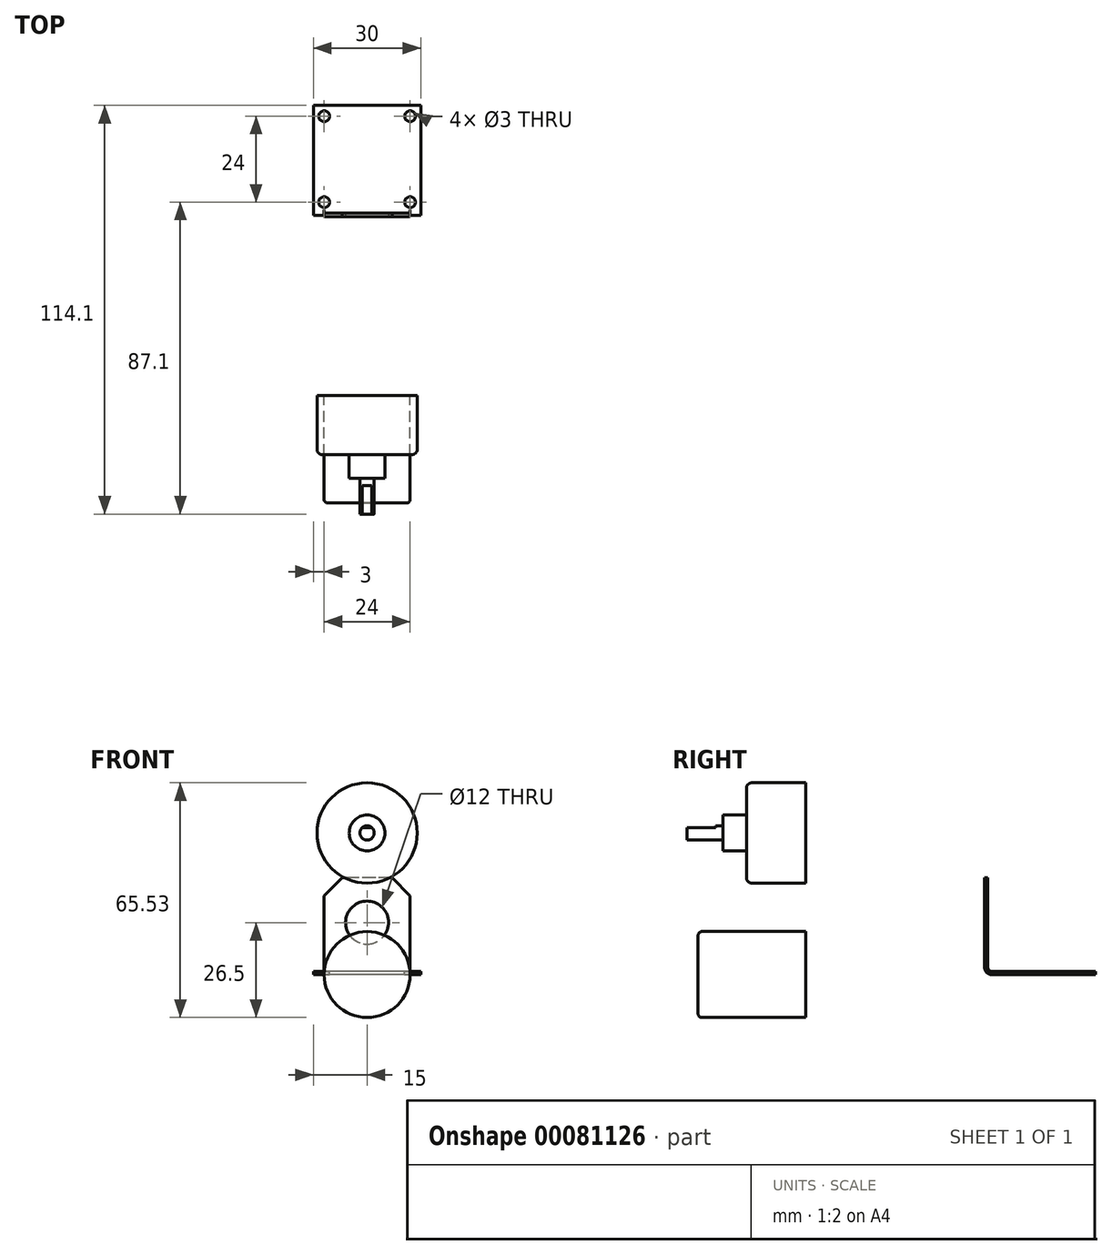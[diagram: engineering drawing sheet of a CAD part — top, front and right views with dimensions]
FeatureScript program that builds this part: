
annotation { "Feature Type Name" : "Feature", "Feature Type Description" : "" }
export const myFeature = defineFeature(function(context is Context, id is Id, definition is map)
    precondition{}
    {
        {
            var Q0;
            Q0=qCreatedBy(makeId("Front.planeOp"),FACE);
            var sketch = newSketch(context, id + "F0", { "sketchPlane" : qUnion([Q0])});
            skCircle(sketch, "E0", {"center": v(0, 0) * mm, "radius": 12 * mm});
            skSolve(sketch);
        }
        {
            var Q0;
            Q0=makeQuery(id+"F0.imprint","IMPRINT",FACE,{"disambiguationData":[TD([[makeQuery(id+"F0.imprint","IMPRINT",EDGE,{"derivedFrom":sQuery(id+"F0.wireOp",EDGE,"E0")}),1.0]])]});
            extrude(context, id + "F1", {"entities" : qUnion([Q0]), "depth" : 30 * mm});
        }
        {
            var Q0;
            Q0=makeQuery(id+"F1.opExtrude","CAP_EDGE",EDGE,{"disambiguationData":[OSD([sQuery(id+"F0.wireOp",EDGE,"E0")])],"isStart":false});
            fillet(context, id + "F2", {"entities" : qUnion([Q0]), "radius" : 1 * mm, "tangentPropagation" : true, "allowEdgeOverflow" : false});
        }
        {
            var Q0;
            Q0=qCreatedBy(makeId("Right.planeOp"),FACE);
            var sketch = newSketch(context, id + "F3", { "sketchPlane" : qUnion([Q0])});
            skLineSegment(sketch, "E1", {"start": v(81, 0) * mm, "end": v(51.9, 0) * mm});
            skLineSegment(sketch, "E2", {"start": v(50, 1.9) * mm, "end": v(50, 27) * mm});
            skLineSegment(sketch, "E3", {"start": v(50, 27) * mm, "end": v(50.9, 27) * mm});
            skLineSegment(sketch, "E4", {"start": v(50.9, 27) * mm, "end": v(50.9, 1.9) * mm});
            skLineSegment(sketch, "E5", {"start": v(51.9, 0.9) * mm, "end": v(81, 0.9) * mm});
            skLineSegment(sketch, "E6", {"start": v(81, 0.9) * mm, "end": v(81, 0) * mm});
            skPoint(sketch, "E7.visualSharp", {"position": v(50.9, 0.9) * mm});
            skArc(sketch, "E7.filletArc", {"start": v(50.9, 1.9) * mm, "mid": v(51.2, 1.2) * mm, "end": v(51.9, 0.9) * mm});
            skPoint(sketch, "E8.visualSharp", {"position": v(50, 0) * mm});
            skArc(sketch, "E8.filletArc", {"start": v(50, 1.9) * mm, "mid": v(50.56, 0.56) * mm, "end": v(51.9, 0) * mm});
            skLineSegment(sketch, "E9", {"start": v(0, 39.53) * mm, "end": v(-33.1, 39.53) * mm});
            skLineSegment(sketch, "E10", {"start": v(-33.1, 39.53) * mm, "end": v(-33.1, 41.53) * mm});
            skLineSegment(sketch, "E11", {"start": v(-33.1, 41.53) * mm, "end": v(-23.1, 41.53) * mm});
            skLineSegment(sketch, "E12", {"start": v(-23.1, 41.53) * mm, "end": v(-23.1, 44.53) * mm});
            skLineSegment(sketch, "E13", {"start": v(-23.1, 44.53) * mm, "end": v(-16.5, 44.53) * mm});
            skLineSegment(sketch, "E14", {"start": v(-16.5, 44.53) * mm, "end": v(-16.5, 53.53) * mm});
            skLineSegment(sketch, "E15", {"start": v(-16.5, 53.53) * mm, "end": v(0, 53.53) * mm});
            skLineSegment(sketch, "E16", {"start": v(0, 53.53) * mm, "end": v(0, 39.53) * mm});
            skSolve(sketch);
        }
        {
            var Q0;
            Q0=makeQuery(id+"F3.imprint","IMPRINT",FACE,{"disambiguationData":[TD([[makeQuery(id+"F3.imprint","IMPRINT",EDGE,{"derivedFrom":sQuery(id+"F3.wireOp",EDGE,"E1")}),-1.0]])]});
            extrude(context, id + "F4", {"entities" : qUnion([Q0]), "depth" : 30 * mm, "symmetric" : true});
        }
        {
            var Q0;
            Q0=makeQuery(id+"F4.opExtrude","SWEPT_FACE",FACE,{"disambiguationData":[OSD([sQuery(id+"F3.wireOp",EDGE,"E5")])]});
            var sketch = newSketch(context, id + "F5", { "sketchPlane" : qUnion([Q0])});
            skLineSegment(sketch, "E17.bottom", {"start": v(-12, 78) * mm, "end": v(12, 78) * mm, "construction": true});
            skLineSegment(sketch, "E17.top", {"start": v(-12, 54) * mm, "end": v(12, 54) * mm, "construction": true});
            skLineSegment(sketch, "E17.left", {"start": v(-12, 78) * mm, "end": v(-12, 54) * mm, "construction": true});
            skLineSegment(sketch, "E17.right", {"start": v(12, 78) * mm, "end": v(12, 54) * mm, "construction": true});
            skCircle(sketch, "E18", {"center": v(-12, 78) * mm, "radius": 1.5 * mm});
            skCircle(sketch, "E19", {"center": v(12, 78) * mm, "radius": 1.5 * mm});
            skCircle(sketch, "E20", {"center": v(-12, 54) * mm, "radius": 1.5 * mm});
            skCircle(sketch, "E21", {"center": v(12, 54) * mm, "radius": 1.5 * mm});
            skLineSegment(sketch, "E22", {"start": v(0, 81) * mm, "end": v(0, 78) * mm, "construction": true});
            skPoint(sketch, "E22.endSnap0", {"position": v(0, 81) * mm});
            skSolve(sketch);
        }
        {
            var Q0;
            Q0=makeQuery(id+"F5.imprint","IMPRINT",FACE,{"disambiguationData":[TD([[makeQuery(id+"F5.imprint","IMPRINT",EDGE,{"derivedFrom":sQuery(id+"F5.wireOp",EDGE,"E18")}),1.0]])]});
            var Q1;
            Q1=makeQuery(id+"F5.imprint","IMPRINT",FACE,{"disambiguationData":[TD([[makeQuery(id+"F5.imprint","IMPRINT",EDGE,{"derivedFrom":sQuery(id+"F5.wireOp",EDGE,"E19")}),1.0]])]});
            var Q2;
            Q2=makeQuery(id+"F5.imprint","IMPRINT",FACE,{"disambiguationData":[TD([[makeQuery(id+"F5.imprint","IMPRINT",EDGE,{"derivedFrom":sQuery(id+"F5.wireOp",EDGE,"E20")}),1.0]])]});
            var Q3;
            Q3=makeQuery(id+"F5.imprint","IMPRINT",FACE,{"disambiguationData":[TD([[makeQuery(id+"F5.imprint","IMPRINT",EDGE,{"derivedFrom":sQuery(id+"F5.wireOp",EDGE,"E21")}),1.0]])]});
            extrude(context, id + "F6", {"entities" : qUnion([Q0, Q1, Q2, Q3]), "operationType" : NewBodyOperationType.REMOVE, "endBound" : BoundingType.THROUGH_ALL, "oppositeDirection" : true, "depth" : 25 * mm});
        }
        {
            var Q0;
            Q0=makeQuery(id+"F4.opExtrude","SWEPT_FACE",FACE,{"disambiguationData":[OSD([sQuery(id+"F3.wireOp",EDGE,"E2")])]});
            var sketch = newSketch(context, id + "F7", { "sketchPlane" : qUnion([Q0])});
            skLineSegment(sketch, "E23", {"start": v(-15, 27) * mm, "end": v(-7, 27) * mm});
            skLineSegment(sketch, "E24", {"start": v(-7, 27) * mm, "end": v(-12, 22) * mm});
            skLineSegment(sketch, "E25", {"start": v(-12, 22) * mm, "end": v(-12, 0.9) * mm});
            skLineSegment(sketch, "E26", {"start": v(-12, 0.9) * mm, "end": v(-15, 0.9) * mm});
            skLineSegment(sketch, "E27", {"start": v(-15, 0.9) * mm, "end": v(-15, 27) * mm});
            skLineSegment(sketch, "E28.MirrorCS", {"start": v(15, 27) * mm, "end": v(7, 27) * mm});
            skLineSegment(sketch, "E29.MirrorCS", {"start": v(15, 0.9) * mm, "end": v(15, 27) * mm});
            skLineSegment(sketch, "E30.MirrorCS", {"start": v(12, 22) * mm, "end": v(12, 0.9) * mm});
            skLineSegment(sketch, "E31.MirrorCS", {"start": v(12, 0.9) * mm, "end": v(15, 0.9) * mm});
            skLineSegment(sketch, "E32.MirrorCS", {"start": v(7, 27) * mm, "end": v(12, 22) * mm});
            skCircle(sketch, "E33", {"center": v(0, 14.5) * mm, "radius": 6 * mm});
            skSolve(sketch);
        }
        {
            var Q0;
            {var subQ3=sQuery(id+"F7.wireOp",EDGE,"E23");Q0=makeQuery(id+"F7.imprint","IMPRINT",FACE,{"disambiguationData":[TD([[makeQuery(id+"F7.imprint","IMPRINT",EDGE,{"derivedFrom":subQ3}),1.0]])]});}
            var Q1;
            {var subQ6=sQuery(id+"F7.wireOp",EDGE,"E28.MirrorCS");Q1=makeQuery(id+"F7.imprint","IMPRINT",FACE,{"disambiguationData":[TD([[makeQuery(id+"F7.imprint","IMPRINT",EDGE,{"derivedFrom":subQ6}),1.0]])]});}
            var Q2;
            {var subQ0=sQuery(id+"F7.wireOp",EDGE,"E26");Q2=makeQuery(id+"F7.imprint","IMPRINT",FACE,{"disambiguationData":[TD([[makeQuery(id+"F7.imprint","IMPRINT",EDGE,{"derivedFrom":subQ0}),-1.0]])]});}
            var Q3;
            {var subQ3=sQuery(id+"F7.wireOp",EDGE,"E31.MirrorCS");Q3=makeQuery(id+"F7.imprint","IMPRINT",FACE,{"disambiguationData":[TD([[makeQuery(id+"F7.imprint","IMPRINT",EDGE,{"derivedFrom":subQ3}),1.0]])]});}
            var Q4;
            Q4=makeQuery(id+"F7.imprint","IMPRINT",FACE,{"disambiguationData":[TD([[makeQuery(id+"F7.imprint","IMPRINT",EDGE,{"derivedFrom":sQuery(id+"F7.wireOp",EDGE,"E33")}),1.0]])]});
            extrude(context, id + "F8", {"entities" : qUnion([Q0, Q1, Q2, Q3, Q4]), "operationType" : NewBodyOperationType.REMOVE, "endBound" : BoundingType.THROUGH_ALL, "oppositeDirection" : true, "depth" : 25 * mm});
        }
        {
            var Q0;
            Q0=makeQuery(id+"F3.imprint","IMPRINT",FACE,{"disambiguationData":[TD([[makeQuery(id+"F3.imprint","IMPRINT",EDGE,{"derivedFrom":sQuery(id+"F3.wireOp",EDGE,"E9")}),-1.0]])]});
            var Q1;
            Q1=sQuery(id+"F3.wireOp",EDGE,"E9");
            revolve(context, id + "F9", {"entities" : qUnion([Q0]), "axis" : qUnion([Q1]), "revolveType" : RevolveType.FULL});
        }
        {
            var Q0;
            Q0=qCreatedBy(makeId("Right.planeOp"),FACE);
            var sketch = newSketch(context, id + "F10", { "sketchPlane" : qUnion([Q0])});
            skLineSegment(sketch, "E34.bottom", {"start": v(-33.1, 41.53) * mm, "end": v(-25.1, 41.53) * mm});
            skLineSegment(sketch, "E34.top", {"start": v(-33.1, 41.03) * mm, "end": v(-25.1, 41.03) * mm});
            skLineSegment(sketch, "E34.left", {"start": v(-33.1, 41.53) * mm, "end": v(-33.1, 41.03) * mm});
            skLineSegment(sketch, "E34.right", {"start": v(-25.1, 41.53) * mm, "end": v(-25.1, 41.03) * mm});
            skSolve(sketch);
        }
        {
            var Q0;
            Q0=makeQuery(id+"F10.imprint","IMPRINT",FACE,{"disambiguationData":[TD([[makeQuery(id+"F10.imprint","IMPRINT",EDGE,{"derivedFrom":sQuery(id+"F10.wireOp",EDGE,"E34.bottom")}),-1.0]])]});
            extrude(context, id + "F11", {"entities" : qUnion([Q0]), "operationType" : NewBodyOperationType.REMOVE, "oppositeDirection" : true, "depth" : 25 * mm, "symmetric" : true});
        }
        {
            var Q0;
            Q0=makeQuery(id+"F9.opRevolve","SWEPT_EDGE",EDGE,{"disambiguationData":[OSD([sQuery(id+"F3.wireOp",EDGE,"E14"),sQuery(id+"F3.wireOp",EDGE,"E15")])]});
            fillet(context, id + "F12", {"entities" : qUnion([Q0]), "radius" : 1.5 * mm, "tangentPropagation" : true, "allowEdgeOverflow" : false});
        }
    });
